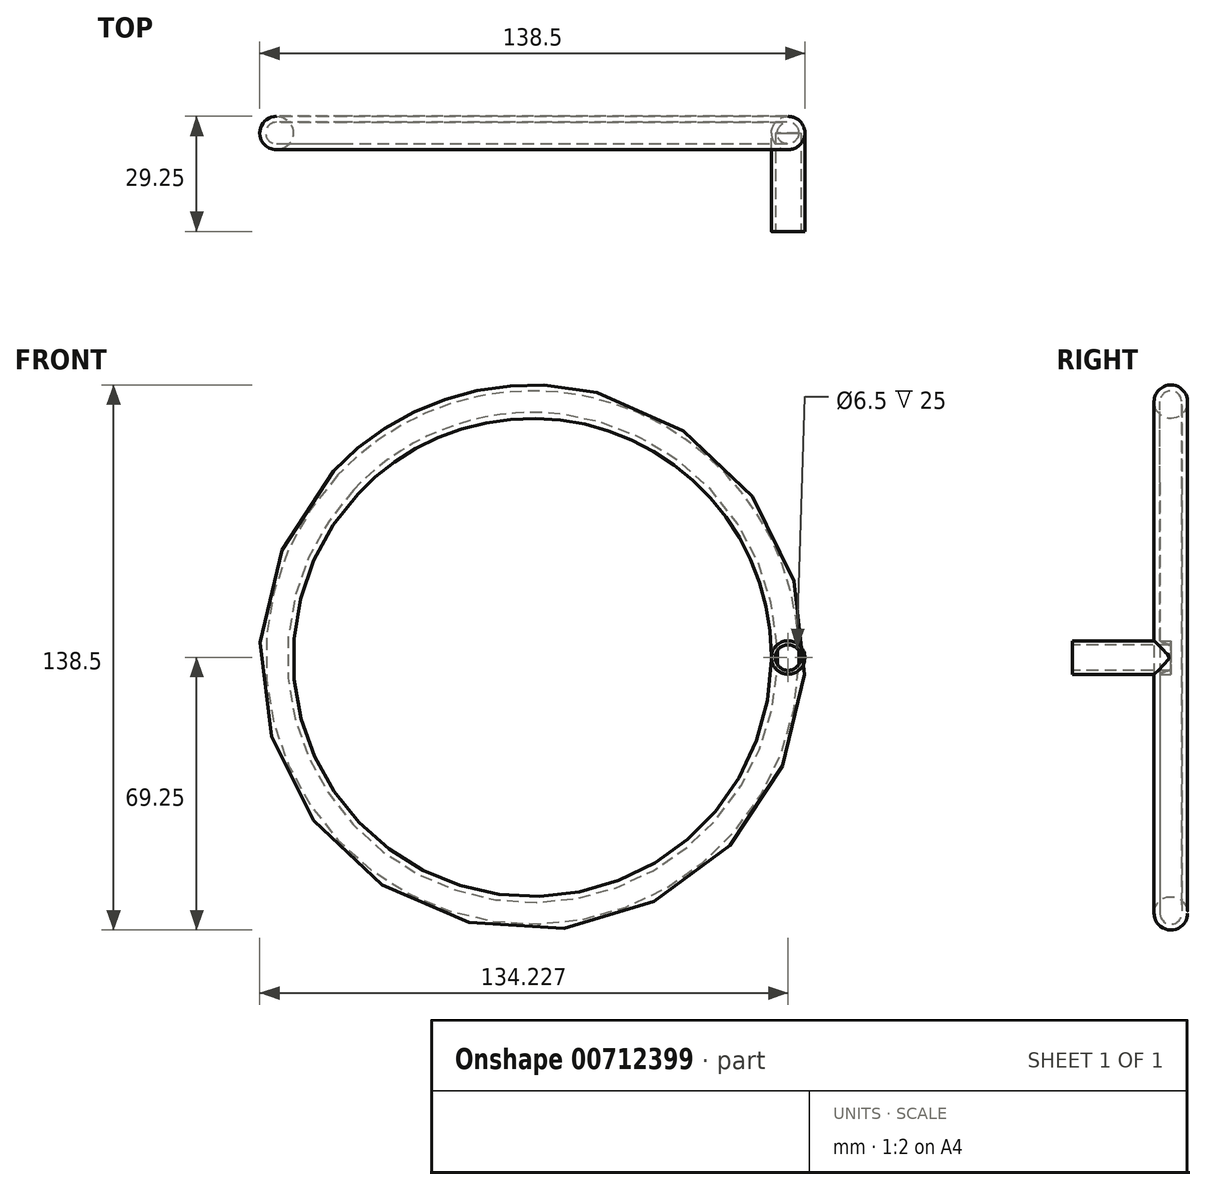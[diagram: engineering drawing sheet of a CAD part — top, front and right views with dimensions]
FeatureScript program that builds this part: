
annotation { "Feature Type Name" : "Feature", "Feature Type Description" : "" }
export const myFeature = defineFeature(function(context is Context, id is Id, definition is map)
    precondition{}
    {
        {
            var Q0;
            Q0=qCreatedBy(makeId("Front.planeOp"),FACE);
            var sketch = newSketch(context, id + "F0", { "sketchPlane" : qUnion([Q0])});
            skCircle(sketch, "E0", {"center": v(0, 0) * mm, "radius": 65 * mm});
            skSolve(sketch);
        }
        {
            var Q0;
            Q0=qCreatedBy(makeId("Top.planeOp"),FACE);
            var sketch = newSketch(context, id + "F1", { "sketchPlane" : qUnion([Q0])});
            skCircle(sketch, "E1", {"center": v(65, 0) * mm, "radius": 4.25 * mm});
            skCircle(sketch, "E2", {"center": v(65, 0) * mm, "radius": 2.75 * mm});
            skSolve(sketch);
        }
        {
            var Q0;
            Q0=makeQuery(id+"F1.imprint","IMPRINT",FACE,{"disambiguationData":[TD([[makeQuery(id+"F1.imprint","IMPRINT",EDGE,{"derivedFrom":sQuery(id+"F1.wireOp",EDGE,"E1")}),1.0]])]});
            var Q1;
            Q1=sQuery(id+"F0.wireOp",EDGE,"E0");
            sweep(context, id + "F2", {"profiles" : qUnion([Q0]), "path" : qUnion([Q1])});
        }
        {
            var Q0;
            Q0=qCreatedBy(makeId("Front.planeOp"),FACE);
            var sketch = newSketch(context, id + "F3", { "sketchPlane" : qUnion([Q0])});
            skCircle(sketch, "E3", {"center": v(64.98, 0) * mm, "radius": 4.25 * mm});
            skSolve(sketch);
        }
        {
            var Q0;
            Q0 = qSketchRegion(id + "F3", true);
            extrude(context, id + "F4", {"entities" : qUnion([Q0]), "operationType" : NewBodyOperationType.ADD, "depth" : 25 * mm, "offsetDistance" : 25 * mm});
        }
        {
            var Q0;
            Q0=makeQuery(id+"F4.opExtrude","CAP_FACE",FACE,{"disambiguationData":[OSD([sQuery(id+"F3.wireOp",EDGE,"E3")])],"isStart":false});
            var sketch = newSketch(context, id + "F5", { "sketchPlane" : qUnion([Q0])});
            skCircle(sketch, "E4", {"center": v(64.98, 0) * mm, "radius": 3.25 * mm});
            skSolve(sketch);
        }
        {
            var Q0;
            Q0 = qSketchRegion(id + "F5", true);
            extrude(context, id + "F6", {"entities" : qUnion([Q0]), "operationType" : NewBodyOperationType.REMOVE, "oppositeDirection" : true, "depth" : 25 * mm, "offsetDistance" : 25 * mm});
        }
    });
